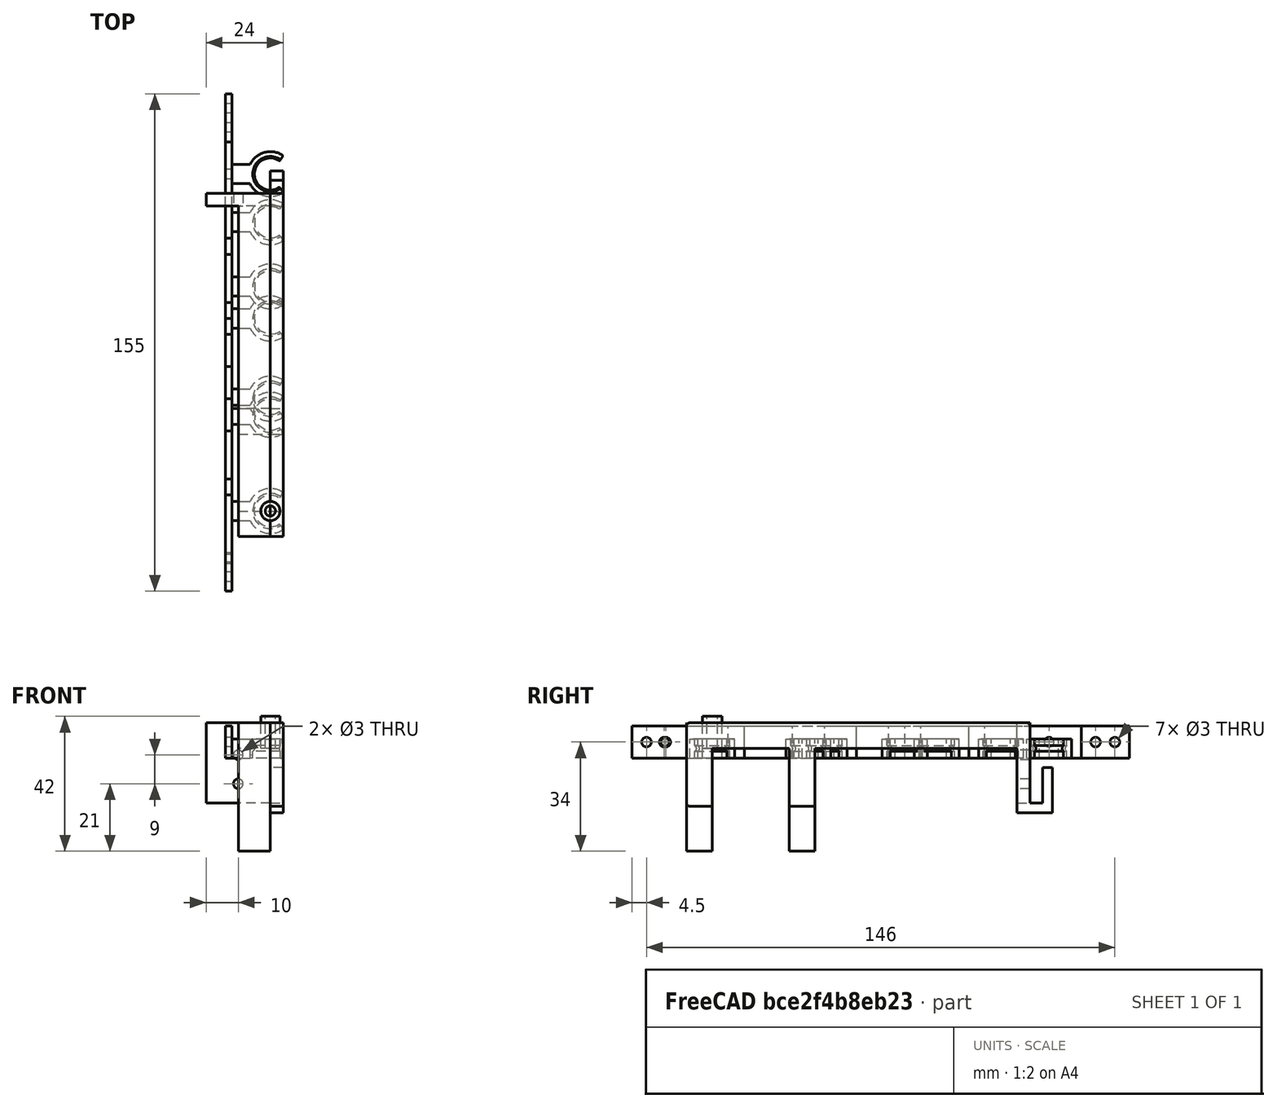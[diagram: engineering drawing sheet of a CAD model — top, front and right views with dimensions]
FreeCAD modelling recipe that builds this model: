
FCSTD DOCUMENT  (FreeCAD 0.16R6707 (Git))
Label: porta_leds
License: All rights reserved
LicenseURL: http://en.wikipedia.org/wiki/All_rights_reserved
objects: Part::Box×18, Part::Cut×16, Part::MultiFuse×15, Part::Feature×12, Part::Cylinder×8, Part::Fillet×7, Part::FeaturePython×4, Part::Torus×3, Part::Mirroring×1
note: 84 computed .brp shape members not serialized (recipe doc carries the construction recipe); baked Part::Feature solids carry a one-line shape summary decoded from their .brp

FEATURE [Part::Cylinder] Cylinder  label="Cilindro"
  Angle = 360
  Height = 36
  Radius = 5.5
FEATURE [Part::Fillet] Fillet
  Base = -> Cylinder
  Edges = 1 edges r=4: [Edge1]
FEATURE [Part::Torus] Torus  label="Toro"
  Angle1 = -180
  Angle2 = 180
  Angle3 = 360
  Placement = pos=(0,0,26) rot=(0,0,1;0rad)
  Radius1 = 6
  Radius2 = 1
FEATURE [Part::Cut] Cut  label="led"
  Base = -> Fillet
  Tool = -> Torus
FEATURE [Part::Cylinder] Cylinder002  label="Cilindro002"
  Angle = 250
  Height = 6
  Placement = pos=(0,0,4) rot=(0,0,1;0rad)
  Radius = 7
FEATURE [Part::Fillet] Fillet001
  Base = -> Cylinder002
  Edges = 2 edges r=0.5: [Edge2,Edge4]
  Placement = pos=(0,0,19) rot=(0,0,1;0rad)
FEATURE [Part::Cut] Cut001  label="anilla"
  Base = -> Fillet001
  Placement = pos=(0,0,-26) rot=(0,0,1;0.959931rad)
  Tool = -> Cut
FEATURE [Part::Box] Box  label="Cubo"
  Height = 6
  Length = 8
  Placement = pos=(-14,-3,-3) rot=(0,0,1;0rad)
  Width = 6
FEATURE [Part::MultiFuse] Fusion
  Shapes = -> [Box,Cut001]
FEATURE [Part::Box] Box001  label="Cubo001"
  Height = 10
  Length = 2
  Placement = pos=(-14,-25,-3) rot=(0,0,1;0rad)
  Width = 50
FEATURE [Part::MultiFuse] Fusion001  label="eslabon"
  Shapes = -> [Box001,Fusion]
FEATURE [Part::FeaturePython] Clone  label="Clone of eslabon"  # Draft clone (typed FeaturePython)
  Objects = -> [Fusion001]
  Scale = (1,1,1)
FEATURE [Part::FeaturePython] Array  # Draft array (typed FeaturePython)
  Angle = 360
  ArrayType = 0
  Axis = (0,0,1)
  Base = -> Fusion001
  Center = (0,0,0)
  Fuse = false
  IntervalAxis = (0,0,0)
  IntervalX = (1,0,0)
  IntervalY = (0,30,0)
  IntervalZ = (0,0,0)
  NumberPolar = 1
  NumberX = 1
  NumberY = 4
  NumberZ = 1
FEATURE [Part::Feature] Part__Feature  label="Chamfer001"
  Placement = pos=(-11,-15,0) rot=(0,1,0;1.5708rad)
  shape: bbox 15 x 5.5 x 5.5 mm, 16 faces (baked)
FEATURE [Part::Feature] Part__Feature001  label="Chamfer002"
  Placement = pos=(-11,105,0) rot=(0,1,0;1.5708rad)
  shape: bbox 15 x 5.5 x 5.5 mm, 16 faces (baked)
FEATURE [Part::MultiFuse] Fusion002  label="tornillería"
  Placement = pos=(0,0,2) rot=(0,0,1;0rad)
  Shapes = -> [Part__Feature,Part__Feature001]
FEATURE [Part::Cut] Cut002  label="panel_1"
  Base = -> Array
  Tool = -> Fusion002
FEATURE [Part::Cylinder] Cylinder003  label="Cilindro003"
  Angle = 360
  Height = 36
  Radius = 5.5
FEATURE [Part::Fillet] Fillet002
  Base = -> Cylinder003
  Edges = 1 edges r=4: [Edge1]
FEATURE [Part::Torus] Torus001  label="Toro001"
  Angle1 = -180
  Angle2 = 180
  Angle3 = 360
  Placement = pos=(0,0,26) rot=(0,0,1;0rad)
  Radius1 = 6
  Radius2 = 1
FEATURE [Part::Cut] Cut003  label="led001"
  Base = -> Fillet002
  Tool = -> Torus001
FEATURE [Part::Cylinder] Cylinder004  label="Cilindro004"
  Angle = 250
  Height = 6
  Placement = pos=(0,0,4) rot=(0,0,1;0rad)
  Radius = 7
FEATURE [Part::Fillet] Fillet003
  Base = -> Cylinder004
  Edges = 2 edges r=0.5: [Edge2,Edge4]
  Placement = pos=(0,0,19) rot=(0,0,1;0rad)
FEATURE [Part::Cut] Cut004  label="anilla001"
  Base = -> Fillet003
  Placement = pos=(0,0,-26) rot=(0,0,1;0.959931rad)
  Tool = -> Cut003
FEATURE [Part::Box] Box002  label="Cubo002"
  Height = 6
  Length = 8
  Placement = pos=(-14,-3,-3) rot=(0,0,1;0rad)
  Width = 6
FEATURE [Part::MultiFuse] Fusion003
  Shapes = -> [Box002,Cut004]
FEATURE [Part::Box] Box003  label="Cubo003"
  Height = 10
  Length = 2
  Placement = pos=(-14,-25,-3) rot=(0,0,1;0rad)
  Width = 50
FEATURE [Part::MultiFuse] Fusion004  label="eslabon001"
  Shapes = -> [Box003,Fusion003]
FEATURE [Part::FeaturePython] Array001  # Draft array (typed FeaturePython)
  Angle = 360
  ArrayType = 0
  Axis = (0,0,1)
  Base = -> Fusion004
  Center = (0,0,0)
  Fuse = false
  IntervalAxis = (0,0,0)
  IntervalX = (1,0,0)
  IntervalY = (0,30,0)
  IntervalZ = (0,0,0)
  NumberPolar = 1
  NumberX = 1
  NumberY = 1
  NumberZ = 1
FEATURE [Part::Feature] Part__Feature002  label="Chamfer003"
  Placement = pos=(-11,-15,0) rot=(0,1,0;1.5708rad)
  shape: bbox 15 x 5.5 x 5.5 mm, 16 faces (baked)
FEATURE [Part::Feature] Part__Feature003  label="Chamfer004"
  Placement = pos=(-11,105,0) rot=(0,1,0;1.5708rad)
  shape: bbox 15 x 5.5 x 5.5 mm, 16 faces (baked)
FEATURE [Part::MultiFuse] Fusion005  label="tornillería001"
  Placement = pos=(0,0,2) rot=(0,0,1;0rad)
  Shapes = -> [Part__Feature002,Part__Feature003]
FEATURE [Part::Cut] Cut005  label="panel_002"
  Base = -> Array001
  Tool = -> Fusion005
FEATURE [Part::Cylinder] Cylinder005  label="Cilindro005"
  Angle = 360
  Height = 36
  Radius = 5.5
FEATURE [Part::Fillet] Fillet004
  Base = -> Cylinder005
  Edges = 1 edges r=4: [Edge1]
FEATURE [Part::Torus] Torus002  label="Toro002"
  Angle1 = -180
  Angle2 = 180
  Angle3 = 360
  Placement = pos=(0,0,26) rot=(0,0,1;0rad)
  Radius1 = 6
  Radius2 = 1
FEATURE [Part::Cut] Cut006  label="led002"
  Base = -> Fillet004
  Tool = -> Torus002
FEATURE [Part::Cylinder] Cylinder006  label="Cilindro006"
  Angle = 250
  Height = 6
  Placement = pos=(0,0,4) rot=(0,0,1;0rad)
  Radius = 7
FEATURE [Part::Fillet] Fillet005
  Base = -> Cylinder006
  Edges = 2 edges r=0.5: [Edge2,Edge4]
  Placement = pos=(0,0,19) rot=(0,0,1;0rad)
FEATURE [Part::Cut] Cut007  label="anilla002"
  Base = -> Fillet005
  Placement = pos=(0,0,-26) rot=(0,0,1;0.959931rad)
  Tool = -> Cut006
FEATURE [Part::Box] Box004  label="Cubo004"
  Height = 6
  Length = 8
  Placement = pos=(-14,-3,-3) rot=(0,0,1;0rad)
  Width = 6
FEATURE [Part::MultiFuse] Fusion006
  Shapes = -> [Box004,Cut007]
FEATURE [Part::Box] Box005  label="Cubo005"
  Height = 10
  Length = 2
  Placement = pos=(-14,-25,-3) rot=(0,0,1;0rad)
  Width = 50
FEATURE [Part::MultiFuse] Fusion007  label="eslabon002"
  Shapes = -> [Box005,Fusion006]
FEATURE [Part::FeaturePython] Array002  # Draft array (typed FeaturePython)
  Angle = 360
  ArrayType = 0
  Axis = (0,0,1)
  Base = -> Fusion007
  Center = (0,0,0)
  Fuse = false
  IntervalAxis = (0,0,0)
  IntervalX = (1,0,0)
  IntervalY = (0,35,0)
  IntervalZ = (0,0,0)
  NumberPolar = 1
  NumberX = 1
  NumberY = 4
  NumberZ = 1
FEATURE [Part::Feature] Part__Feature004  label="Chamfer005"
  Placement = pos=(-11,-20.5,0) rot=(0,1,0;1.5708rad)
  shape: bbox 15 x 5.5 x 5.5 mm, 16 faces (baked)
FEATURE [Part::Feature] Part__Feature005  label="Chamfer006"
  Placement = pos=(-11,125.5,0) rot=(0,1,0;1.5708rad)
  shape: bbox 15 x 5.5 x 5.5 mm, 16 faces (baked)
FEATURE [Part::Feature] Part__Feature006  label="Chamfer007"
  Placement = pos=(-11,-14.5,0) rot=(0,1,0;1.5708rad)
  shape: bbox 15 x 5.5 x 5.5 mm, 16 faces (baked)
FEATURE [Part::Feature] Part__Feature007  label="Chamfer008"
  Placement = pos=(-11,119.5,0) rot=(0,1,0;1.5708rad)
  shape: bbox 15 x 5.5 x 5.5 mm, 16 faces (baked)
FEATURE [Part::MultiFuse] Fusion008  label="tornillería3"
  Placement = pos=(0,0,2) rot=(0,0,1;0rad)
  Shapes = -> [Part__Feature004,Part__Feature006,Part__Feature005,Part__Feature007]
FEATURE [Part::Cut] Cut008
  Base = -> Array002
  Tool = -> Fusion008
FEATURE [Part::Box] Box006  label="Cubo006"
  Height = 300
  Length = 700
  Placement = pos=(0,0,-300) rot=(0,0,1;0rad)
  Width = 24
FEATURE [Part::Box] Box007  label="Cubo007"
  Height = 40
  Length = 10
  Placement = pos=(0,-8,-32) rot=(0,0,1;0rad)
  Width = 40
FEATURE [Part::Cut] Cut009
  Base = -> Box007
  Tool = -> Box006
FEATURE [Part::Box] Box008  label="Cubo008"
  Height = 8
  Length = 10
  Placement = pos=(0,32,0) rot=(0,0,1;0rad)
  Width = 63
FEATURE [Part::Box] Box009  label="Cubo009"
  Height = 25
  Length = 20
  Placement = pos=(0,0,-25) rot=(0,0,1;0rad)
  Width = 4
FEATURE [Part::Feature] Part__Feature008  label="Chamfer009"
  Placement = pos=(10,6,-19) rot=(-1,0,0;1.5708rad)
  shape: bbox 5.5 x 15 x 5.5 mm, 16 faces (baked)
FEATURE [Part::Feature] Part__Feature009  label="Chamfer010"
  Placement = pos=(10,6,-10) rot=(-1,0,0;1.5708rad)
  shape: bbox 5.5 x 15 x 5.5 mm, 16 faces (baked)
FEATURE [Part::MultiFuse] Fusion009
  Shapes = -> [Part__Feature008,Part__Feature009]
FEATURE [Part::Cut] Cut010
  Base = -> Box009
  Placement = pos=(0,95,8) rot=(0,0,1;0rad)
  Tool = -> Fusion009
FEATURE [Part::MultiFuse] Fusion010
  Shapes = -> [Cut009,Box008,Cut010]
FEATURE [Part::Mirroring] Part__Mirroring  label="Fusion010 (Mirror #1)"
  Base = (0,0,0)
  Normal = (1,0,0)
  Source = -> Fusion010
FEATURE [Part::Cylinder] Cylinder007  label="Cilindro007"
  Angle = 360
  Height = 10
  Radius = 3
FEATURE [Part::Cylinder] Cylinder008  label="Cilindro008"
  Angle = 360
  Height = 12
  Placement = pos=(0,0,-1) rot=(0,0,1;0rad)
  Radius = 1.6
FEATURE [Part::Cut] Cut011
  Base = -> Cylinder007
  Tool = -> Cylinder008
FEATURE [Part::Box] Box010  label="Cubo010"
  Height = 300
  Length = 700
  Placement = pos=(0,0,-300) rot=(0,0,1;0rad)
  Width = 24
FEATURE [Part::Box] Box011  label="Cubo011"
  Height = 40
  Length = 10
  Placement = pos=(0,-8,-32) rot=(0,0,1;0rad)
  Width = 40
FEATURE [Part::Cut] Cut012
  Base = -> Box011
  Tool = -> Box010
FEATURE [Part::Box] Box012  label="Cubo012"
  Height = 8
  Length = 10
  Placement = pos=(0,32,0) rot=(0,0,1;0rad)
  Width = 63
FEATURE [Part::Box] Box013  label="Cubo013"
  Height = 25
  Length = 20
  Placement = pos=(0,0,-25) rot=(0,0,1;0rad)
  Width = 4
FEATURE [Part::Feature] Part__Feature010  label="Chamfer011"
  Placement = pos=(10,6,-19) rot=(-1,0,0;1.5708rad)
  shape: bbox 5.5 x 15 x 5.5 mm, 16 faces (baked)
FEATURE [Part::Feature] Part__Feature011  label="Chamfer012"
  Placement = pos=(10,6,-10) rot=(-1,0,0;1.5708rad)
  shape: bbox 5.5 x 15 x 5.5 mm, 16 faces (baked)
FEATURE [Part::MultiFuse] Fusion011
  Shapes = -> [Part__Feature010,Part__Feature011]
FEATURE [Part::Cut] Cut013
  Base = -> Box013
  Placement = pos=(0,95,8) rot=(0,0,1;0rad)
  Tool = -> Fusion011
FEATURE [Part::MultiFuse] Fusion012
  Shapes = -> [Cut012,Box012,Cut013]
FEATURE [Part::Box] Box014  label="Cubo014"
  Height = 23
  Length = 12
  Placement = pos=(-1,-18,-41) rot=(0,0,1;0rad)
  Width = 58
FEATURE [Part::Box] Box015  label="Cubo015"
  Height = 48
  Length = 26
  Placement = pos=(4,-17,-25) rot=(0,0,1;0rad)
  Width = 121
FEATURE [Part::MultiFuse] Fusion013
  Shapes = -> [Box015,Box014]
FEATURE [Part::Cut] Cut014
  Base = -> Fusion012
  Tool = -> Fusion013
FEATURE [Part::Box] Box016  label="Cubo016"
  Height = 14
  Length = 4
  Placement = pos=(0,95,-20) rot=(0,0,1;0rad)
  Width = 11
FEATURE [Part::MultiFuse] Fusion014
  Shapes = -> [Cut014,Box016]
FEATURE [Part::Box] Box017  label="Cubo017"
  Height = 16
  Length = 6
  Placement = pos=(-1,99,-17) rot=(0,0,1;0rad)
  Width = 4
FEATURE [Part::Cut] Cut015
  Base = -> Fusion014
  Tool = -> Box017
FEATURE [Part::Fillet] Fillet006
  Base = -> Cut015
  Edges = 3 edges r=1: [Edge42,Edge43,Edge44]
